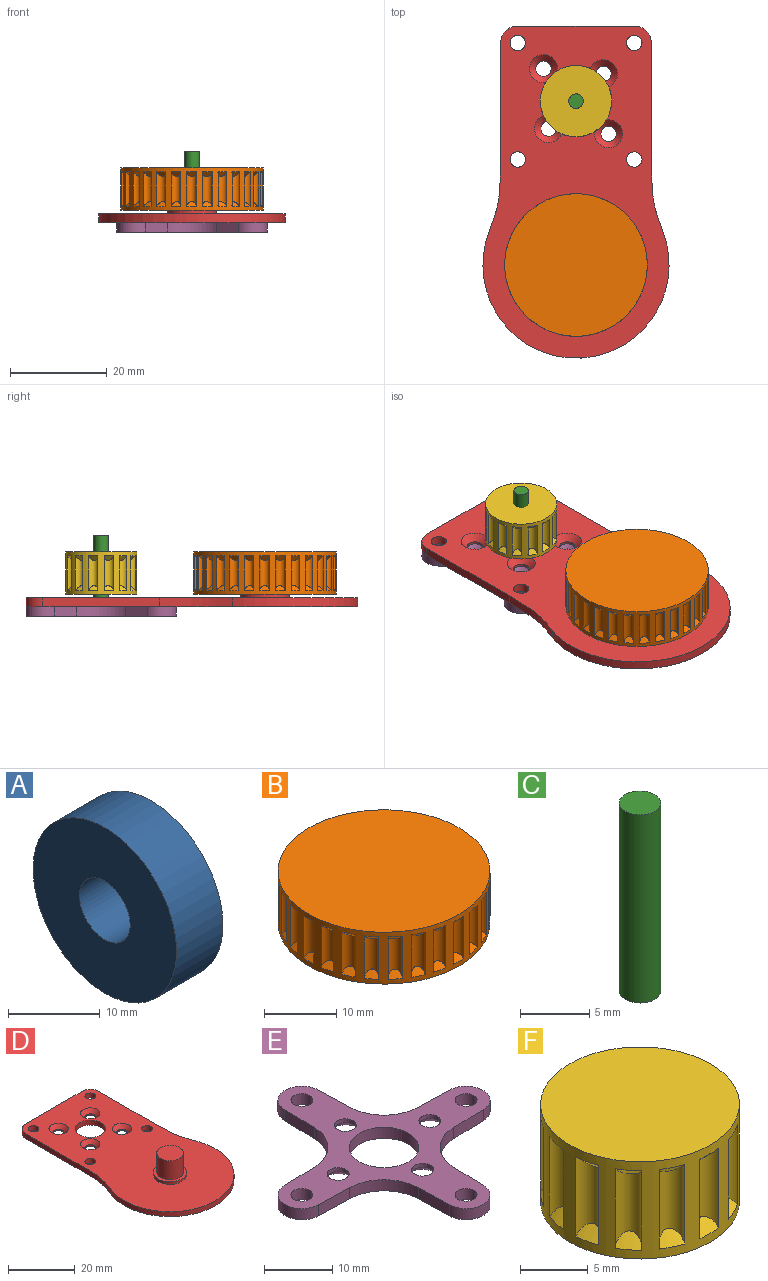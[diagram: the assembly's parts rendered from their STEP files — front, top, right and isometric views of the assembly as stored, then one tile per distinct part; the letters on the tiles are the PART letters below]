
ASSEMBLY  parts=6 mates=5
PART A: 4 faces, bbox 7.2x22.1x22.1 mm
  f0: cylinder r=3.91mm len=7.81mm, axis (-1,0,0), area 175.4mm2, adj f2,f3
  f1: cylinder r=11.05mm len=22.1mm, axis (-1,0,0), area 496.4mm2, adj f2,f3
  f2: plane 22.1x22.1mm, normal (1,0,0), area 335.7mm2, adj f0,f1
  f3: plane 22.1x22.1mm, normal (-1,0,0), area 335.7mm2, adj f0,f1
PART B: 87 faces, bbox 29.4x29.4x8.8 mm
  f0: cylinder r=1mm len=7.2mm, axis (0,0,-1), area 18.2mm2, adj f28,f29,f58
  f1: cylinder r=1mm len=7.2mm, axis (0,0,-1), area 18.2mm2, adj f28,f30,f59
  f2: cylinder r=1mm len=7.2mm, axis (0,0,-1), area 18.2mm2, adj f28,f31,f60
  f3: cylinder r=1mm len=7.2mm, axis (0,0,-1), area 18.2mm2, adj f28,f32,f61
  f4: cylinder r=1mm len=7.2mm, axis (0,0,-1), area 18.2mm2, adj f28,f33,f62
  f5: cylinder r=1mm len=7.2mm, axis (0,0,-1), area 18.2mm2, adj f28,f34,f63
  f6: cylinder r=1mm len=7.2mm, axis (0,0,-1), area 18.2mm2, adj f28,f35,f64
  f7: cylinder r=1mm len=7.2mm, axis (0,0,-1), area 18.2mm2, adj f28,f36,f65
  f8: cylinder r=1mm len=7.2mm, axis (0,0,-1), area 18.2mm2, adj f28,f37,f66
  f9: cylinder r=1mm len=7.2mm, axis (0,0,-1), area 18.2mm2, adj f28,f38,f67
  f10: cylinder r=1mm len=7.2mm, axis (0,0,-1), area 18.2mm2, adj f28,f39,f68
  f11: cylinder r=1mm len=7.2mm, axis (0,0,-1), area 18.2mm2, adj f28,f40,f69
  f12: cylinder r=1mm len=7.2mm, axis (0,0,-1), area 18.2mm2, adj f28,f41,f70
  f13: cylinder r=1mm len=7.2mm, axis (0,0,-1), area 18.2mm2, adj f28,f42,f71
  f14: cylinder r=1mm len=7.2mm, axis (0,0,-1), area 18.2mm2, adj f28,f43,f72
  f15: cylinder r=1mm len=7.2mm, axis (0,0,-1), area 18.2mm2, adj f28,f44,f73
  f16: cylinder r=1mm len=7.2mm, axis (0,0,-1), area 18.2mm2, adj f28,f45,f74
  f17: cylinder r=1mm len=7.2mm, axis (0,0,-1), area 18.2mm2, adj f28,f46,f75
  f18: cylinder r=1mm len=7.2mm, axis (0,0,-1), area 18.2mm2, adj f28,f47,f76
  f19: cylinder r=1mm len=7.2mm, axis (0,0,-1), area 18.2mm2, adj f28,f48,f77
  f20: cylinder r=1mm len=7.2mm, axis (0,0,-1), area 18.2mm2, adj f28,f49,f78
  f21: cylinder r=1mm len=7.2mm, axis (0,0,-1), area 18.2mm2, adj f28,f50,f79
  f22: cylinder r=1mm len=7.2mm, axis (0,0,-1), area 18.2mm2, adj f28,f51,f80
  f23: cylinder r=1mm len=7.2mm, axis (0,0,-1), area 18.2mm2, adj f28,f52,f81
  f24: cylinder r=1mm len=7.2mm, axis (0,0,-1), area 18.2mm2, adj f28,f53,f82
  f25: cylinder r=1mm len=7.2mm, axis (0,0,-1), area 18.2mm2, adj f28,f54,f83
  f26: cylinder r=1mm len=7.2mm, axis (0,0,-1), area 18.2mm2, adj f28,f55,f84
  f27: cylinder r=1mm len=7.2mm, axis (0,0,-1), area 18.2mm2, adj f28,f56,f85
  f28: cylinder r=14.71mm len=29.41mm, axis (0,0,-1), area 409.8mm2, adj f0,f1,f2,f3,f4,f5,f6,f7
  f29: cone r=14.71mm half-angle=45deg, axis (0,0,-1), area 2.2mm2, adj f0,f28
  f30: cone r=14.71mm half-angle=45deg, axis (0,0,-1), area 2.2mm2, adj f1,f28
  f31: cone r=14.71mm half-angle=45deg, axis (0,0,-1), area 2.2mm2, adj f2,f28
  f32: cone r=14.71mm half-angle=45deg, axis (0,0,-1), area 2.2mm2, adj f3,f28
  f33: cone r=14.71mm half-angle=45deg, axis (0,0,-1), area 2.2mm2, adj f4,f28
  f34: cone r=14.71mm half-angle=45deg, axis (0,0,-1), area 2.2mm2, adj f5,f28
  f35: cone r=14.71mm half-angle=45deg, axis (0,0,-1), area 2.2mm2, adj f6,f28
  f36: cone r=14.71mm half-angle=45deg, axis (0,0,-1), area 2.2mm2, adj f7,f28
  f37: cone r=14.71mm half-angle=45deg, axis (0,0,-1), area 2.2mm2, adj f8,f28
  f38: cone r=14.71mm half-angle=45deg, axis (0,0,-1), area 2.2mm2, adj f9,f28
  f39: cone r=14.71mm half-angle=45deg, axis (0,0,-1), area 2.2mm2, adj f10,f28
  f40: cone r=14.71mm half-angle=45deg, axis (0,0,-1), area 2.2mm2, adj f11,f28
  f41: cone r=14.71mm half-angle=45deg, axis (0,0,-1), area 2.2mm2, adj f12,f28
  f42: cone r=14.71mm half-angle=45deg, axis (0,0,-1), area 2.2mm2, adj f13,f28
  f43: cone r=14.71mm half-angle=45deg, axis (0,0,-1), area 2.2mm2, adj f14,f28
  f44: cone r=14.71mm half-angle=45deg, axis (0,0,-1), area 2.2mm2, adj f15,f28
  f45: cone r=14.71mm half-angle=45deg, axis (0,0,-1), area 2.2mm2, adj f16,f28
  f46: cone r=14.71mm half-angle=45deg, axis (0,0,-1), area 2.2mm2, adj f17,f28
  f47: cone r=14.71mm half-angle=45deg, axis (0,0,-1), area 2.2mm2, adj f18,f28
  f48: cone r=14.71mm half-angle=45deg, axis (0,0,-1), area 2.2mm2, adj f19,f28
  f49: cone r=14.71mm half-angle=45deg, axis (0,0,-1), area 2.2mm2, adj f20,f28
  f50: cone r=14.71mm half-angle=45deg, axis (0,0,-1), area 2.2mm2, adj f21,f28
  f51: cone r=14.71mm half-angle=45deg, axis (0,0,-1), area 2.2mm2, adj f22,f28
  f52: cone r=14.71mm half-angle=45deg, axis (0,0,-1), area 2.2mm2, adj f23,f28
  f53: cone r=14.71mm half-angle=45deg, axis (0,0,-1), area 2.2mm2, adj f24,f28
  f54: cone r=14.71mm half-angle=45deg, axis (0,0,-1), area 2.2mm2, adj f25,f28
  f55: cone r=14.71mm half-angle=45deg, axis (0,0,-1), area 2.2mm2, adj f26,f28
  f56: cone r=14.71mm half-angle=45deg, axis (0,0,-1), area 2.2mm2, adj f27,f28
  f57: plane 29.41x29.41mm, normal (0,0,-1), area 679.4mm2, adj f28
  f58: cone r=14.71mm half-angle=45deg, axis (0,0,1), area 2.2mm2, adj f0,f28
  f59: cone r=14.71mm half-angle=45deg, axis (0,0,1), area 2.2mm2, adj f1,f28
  f60: cone r=14.71mm half-angle=45deg, axis (0,0,1), area 2.2mm2, adj f2,f28
  f61: cone r=14.71mm half-angle=45deg, axis (0,0,1), area 2.2mm2, adj f3,f28
  f62: cone r=14.71mm half-angle=45deg, axis (0,0,1), area 2.2mm2, adj f4,f28
  f63: cone r=14.71mm half-angle=45deg, axis (0,0,1), area 2.2mm2, adj f5,f28
  f64: cone r=14.71mm half-angle=45deg, axis (0,0,1), area 2.2mm2, adj f6,f28
  f65: cone r=14.71mm half-angle=45deg, axis (0,0,1), area 2.2mm2, adj f7,f28
  f66: cone r=14.71mm half-angle=45deg, axis (0,0,1), area 2.2mm2, adj f8,f28
  f67: cone r=14.71mm half-angle=45deg, axis (0,0,1), area 2.2mm2, adj f9,f28
  f68: cone r=14.71mm half-angle=45deg, axis (0,0,1), area 2.2mm2, adj f10,f28
  f69: cone r=14.71mm half-angle=45deg, axis (0,0,1), area 2.2mm2, adj f11,f28
  f70: cone r=14.71mm half-angle=45deg, axis (0,0,1), area 2.2mm2, adj f12,f28
  f71: cone r=14.71mm half-angle=45deg, axis (0,0,1), area 2.2mm2, adj f13,f28
  f72: cone r=14.71mm half-angle=45deg, axis (0,0,1), area 2.2mm2, adj f14,f28
  f73: cone r=14.71mm half-angle=45deg, axis (0,0,1), area 2.2mm2, adj f15,f28
  f74: cone r=14.71mm half-angle=45deg, axis (0,0,1), area 2.2mm2, adj f16,f28
  f75: cone r=14.71mm half-angle=45deg, axis (0,0,1), area 2.2mm2, adj f17,f28
  f76: cone r=14.71mm half-angle=45deg, axis (0,0,1), area 2.2mm2, adj f18,f28
  f77: cone r=14.71mm half-angle=45deg, axis (0,0,1), area 2.2mm2, adj f19,f28
  f78: cone r=14.71mm half-angle=45deg, axis (0,0,1), area 2.2mm2, adj f20,f28
  f79: cone r=14.71mm half-angle=45deg, axis (0,0,1), area 2.2mm2, adj f21,f28
  f80: cone r=14.71mm half-angle=45deg, axis (0,0,1), area 2.2mm2, adj f22,f28
  f81: cone r=14.71mm half-angle=45deg, axis (0,0,1), area 2.2mm2, adj f23,f28
  f82: cone r=14.71mm half-angle=45deg, axis (0,0,1), area 2.2mm2, adj f24,f28
  f83: cone r=14.71mm half-angle=45deg, axis (0,0,1), area 2.2mm2, adj f25,f28
  f84: cone r=14.71mm half-angle=45deg, axis (0,0,1), area 2.2mm2, adj f26,f28
  f85: cone r=14.71mm half-angle=45deg, axis (0,0,1), area 2.2mm2, adj f27,f28
  f86: plane 29.41x29.41mm, normal (0,0,1), area 679.4mm2, adj f28
PART C: 3 faces, bbox 3x3x16.6 mm
  f0: cylinder r=1.5mm len=16.6mm, axis (0,0,1), area 156.5mm2, adj f1,f2
  f1: plane 3x3mm, normal (0,0,-1), area 7.1mm2, adj f0
  f2: plane 3x3mm, normal (0,0,1), area 7.1mm2, adj f0
PART D: 27 faces, bbox 38.4x68.5x9.8 mm
  f0: plane 24.04x1.8mm, normal (-1,0,0), area 43.3mm2, adj f1,f14,f17,f18
  f1: extruded ~15.15x2.5mm, area 27.9mm2, adj f0,f2,f17,f18
  f2: cylinder r=19.21mm len=38.41mm, axis (0,0,-1), area 133mm2, adj f1,f3,f17,f18
  f3: extruded ~15.15x2.5mm, area 27.9mm2, adj f2,f4,f17,f18
  f4: plane 24.04x1.8mm, normal (1,0,0), area 43.3mm2, adj f3,f5,f17,f18
  f5: cylinder r=3.5mm len=3.5mm, axis (0,0,-1), area 9.9mm2, adj f4,f6,f17,f18
  f6: plane 24.04x1.8mm, normal (0,1,0), area 43.3mm2, adj f5,f14,f17,f18
  f7: cylinder r=1.6mm len=3.2mm, axis (0,0,-1), area 5mm2, adj f18,f25
  f8: cylinder r=1.6mm len=3.2mm, axis (0,0,-1), area 5mm2, adj f18,f23
  f9: cylinder r=1.6mm len=3.2mm, axis (0,0,-1), area 5mm2, adj f18,f24
  f10: cylinder r=1.6mm len=3.2mm, axis (0,0,-1), area 5mm2, adj f18,f26
  f11: cylinder r=1.6mm len=3.2mm, axis (0,0,-1), area 18.1mm2, adj f17,f18
  f12: cylinder r=1.6mm len=3.2mm, axis (0,0,-1), area 18.1mm2, adj f17,f18
  f13: cylinder r=1.6mm len=3.2mm, axis (0,0,-1), area 18.1mm2, adj f17,f18
  f14: cylinder r=3.5mm len=3.5mm, axis (0,0,-1), area 9.9mm2, adj f0,f6,f17,f18
  f15: cylinder r=1.6mm len=3.2mm, axis (0,0,-1), area 18.1mm2, adj f17,f18
  f16: cylinder r=4.5mm len=9mm, axis (0,0,-1), area 50.9mm2, adj f17,f18
  f17: plane 68.54x38.41mm, normal (0,0,1), area 1889.5mm2, adj f0,f1,f2,f3,f4,f5,f6,f11
  f18: plane 68.54x38.41mm, normal (0,0,-1), area 2041.6mm2, adj f0,f1,f2,f3,f4,f5,f6,f7
  f19: cylinder r=5mm len=10mm, axis (0,0,-1), area 31.4mm2, adj f17,f20
  f20: plane 10x10mm, normal (0,0,1), area 28.3mm2, adj f19,f22
  f21: plane 8x8mm, normal (0,0,1), area 50.3mm2, adj f22
  f22: cylinder r=4mm len=8mm, axis (0,0,-1), area 175.9mm2, adj f20,f21
  f23: cone r=1.6mm half-angle=45deg, axis (0,0,1), area 26mm2, adj f8,f17
  f24: cone r=1.6mm half-angle=45deg, axis (0,0,1), area 26mm2, adj f9,f17
  f25: cone r=1.6mm half-angle=45deg, axis (0,0,1), area 26mm2, adj f7,f17
  f26: cone r=1.6mm half-angle=45deg, axis (0,0,1), area 26mm2, adj f10,f17
PART E: 31 faces, bbox 41x41x2 mm
  f0: cylinder r=3.5mm len=7mm, axis (0,0,-1), area 21.7mm2, adj f1,f24,f25,f26
  f1: plane 6.3x2mm, normal (-1,0.02,0), area 12.6mm2, adj f0,f2,f25,f26
  f2: cylinder r=7.31mm len=7.13mm, axis (0,0,-1), area 22.3mm2, adj f1,f3,f25,f26
  f3: plane 6.3x2mm, normal (-0.02,1,0), area 12.6mm2, adj f2,f4,f25,f26
  f4: cylinder r=3.5mm len=7mm, axis (0,0,-1), area 21.7mm2, adj f3,f5,f25,f26
  f5: plane 6.3x2mm, normal (-0.02,-1,0), area 12.6mm2, adj f4,f6,f25,f26
  f6: cylinder r=7.31mm len=7.13mm, axis (0,0,-1), area 22.3mm2, adj f5,f7,f25,f26
  f7: plane 6.3x2mm, normal (-1,-0.02,0), area 12.6mm2, adj f6,f8,f25,f26
  f8: cylinder r=3.5mm len=7mm, axis (0,0,-1), area 21.7mm2, adj f7,f9,f25,f26
  f9: plane 6.3x2mm, normal (1,-0.02,0), area 12.6mm2, adj f8,f10,f25,f26
  f10: cylinder r=7.31mm len=7.13mm, axis (0,0,-1), area 22.3mm2, adj f9,f11,f25,f26
  f11: plane 6.3x2mm, normal (0.02,-1,0), area 12.6mm2, adj f10,f12,f25,f26
  f12: cylinder r=3.5mm len=7mm, axis (0,0,-1), area 21.7mm2, adj f11,f13,f25,f26
  f13: plane 6.3x2mm, normal (0.02,1,0), area 12.6mm2, adj f12,f14,f25,f26
  f14: cylinder r=7.31mm len=7.13mm, axis (0,0,-1), area 22.3mm2, adj f13,f24,f25,f26
  f15: cylinder r=1.6mm len=3.2mm, axis (0,0,-1), area 7mm2, adj f25,f30
  f16: cylinder r=1.6mm len=3.2mm, axis (0,0,-1), area 7mm2, adj f25,f29
  f17: cylinder r=1.6mm len=3.2mm, axis (0,0,-1), area 20.1mm2, adj f25,f26
  f18: cylinder r=1.6mm len=3.2mm, axis (0,0,-1), area 20.1mm2, adj f25,f26
  f19: cylinder r=5.1mm len=10.2mm, axis (0,0,-1), area 64.1mm2, adj f25,f26
  f20: cylinder r=1.6mm len=3.2mm, axis (0,0,-1), area 20.1mm2, adj f25,f26
  f21: cylinder r=1.6mm len=3.2mm, axis (0,0,-1), area 20.1mm2, adj f25,f26
  f22: cylinder r=1.6mm len=3.2mm, axis (0,0,-1), area 7mm2, adj f25,f27
  f23: cylinder r=1.6mm len=3.2mm, axis (0,0,-1), area 7mm2, adj f25,f28
  f24: plane 6.3x2mm, normal (1,0.02,0), area 12.6mm2, adj f0,f14,f25,f26
  f25: plane 41x41mm, normal (0,0,1), area 416.3mm2, adj f0,f1,f2,f3,f4,f5,f6,f7
  f26: plane 41x41mm, normal (0,0,-1), area 342.7mm2, adj f0,f1,f2,f3,f4,f5,f6,f7
  f27: cone r=2.9mm half-angle=45deg, axis (0,0,-1), area 26mm2, adj f22,f26
  f28: cone r=1.6mm half-angle=45deg, axis (0,0,-1), area 26mm2, adj f23,f26
  f29: cone r=1.6mm half-angle=45deg, axis (0,0,-1), area 26mm2, adj f16,f26
  f30: cone r=2.9mm half-angle=45deg, axis (0,0,-1), area 26mm2, adj f15,f26
PART F: 45 faces, bbox 14.7x14.7x8.8 mm
  f0: cylinder r=1mm len=7.2mm, axis (0,0,-1), area 17.9mm2, adj f14,f15,f30
  f1: cylinder r=1mm len=7.2mm, axis (0,0,-1), area 17.9mm2, adj f14,f16,f31
  f2: cylinder r=1mm len=7.2mm, axis (0,0,-1), area 17.9mm2, adj f14,f17,f32
  f3: cylinder r=1mm len=7.2mm, axis (0,0,-1), area 17.9mm2, adj f14,f18,f33
  f4: cylinder r=1mm len=7.2mm, axis (0,0,-1), area 17.9mm2, adj f14,f19,f34
  f5: cylinder r=1mm len=7.2mm, axis (0,0,-1), area 17.9mm2, adj f14,f20,f35
  f6: cylinder r=1mm len=7.2mm, axis (0,0,-1), area 17.9mm2, adj f14,f21,f36
  f7: cylinder r=1mm len=7.2mm, axis (0,0,-1), area 17.9mm2, adj f14,f22,f37
  f8: cylinder r=1mm len=7.2mm, axis (0,0,-1), area 17.9mm2, adj f14,f23,f38
  f9: cylinder r=1mm len=7.2mm, axis (0,0,-1), area 17.9mm2, adj f14,f24,f39
  f10: cylinder r=1mm len=7.2mm, axis (0,0,-1), area 17.9mm2, adj f14,f25,f40
  f11: cylinder r=1mm len=7.2mm, axis (0,0,-1), area 17.9mm2, adj f14,f26,f41
  f12: cylinder r=1mm len=7.2mm, axis (0,0,-1), area 17.9mm2, adj f14,f27,f42
  f13: cylinder r=1mm len=7.2mm, axis (0,0,-1), area 17.9mm2, adj f14,f28,f43
  f14: cylinder r=7.35mm len=14.71mm, axis (0,0,-1), area 204.8mm2, adj f0,f1,f2,f3,f4,f5,f6,f7
  f15: cone r=7.35mm half-angle=45deg, axis (0,0,-1), area 2.2mm2, adj f0,f14
  f16: cone r=7.35mm half-angle=45deg, axis (0,0,-1), area 2.2mm2, adj f1,f14
  f17: cone r=7.35mm half-angle=45deg, axis (0,0,-1), area 2.2mm2, adj f2,f14
  f18: cone r=7.35mm half-angle=45deg, axis (0,0,-1), area 2.2mm2, adj f3,f14
  f19: cone r=7.35mm half-angle=45deg, axis (0,0,-1), area 2.2mm2, adj f4,f14
  f20: cone r=7.35mm half-angle=45deg, axis (0,0,-1), area 2.2mm2, adj f5,f14
  f21: cone r=7.35mm half-angle=45deg, axis (0,0,-1), area 2.2mm2, adj f6,f14
  f22: cone r=7.35mm half-angle=45deg, axis (0,0,-1), area 2.2mm2, adj f7,f14
  f23: cone r=7.35mm half-angle=45deg, axis (0,0,-1), area 2.2mm2, adj f8,f14
  f24: cone r=7.35mm half-angle=45deg, axis (0,0,-1), area 2.2mm2, adj f9,f14
  f25: cone r=7.35mm half-angle=45deg, axis (0,0,-1), area 2.2mm2, adj f10,f14
  f26: cone r=7.35mm half-angle=45deg, axis (0,0,-1), area 2.2mm2, adj f11,f14
  f27: cone r=7.35mm half-angle=45deg, axis (0,0,-1), area 2.2mm2, adj f12,f14
  f28: cone r=7.35mm half-angle=45deg, axis (0,0,-1), area 2.2mm2, adj f13,f14
  f29: plane 14.71x14.71mm, normal (0,0,-1), area 169.9mm2, adj f14
  f30: cone r=7.35mm half-angle=45deg, axis (0,0,1), area 2.2mm2, adj f0,f14
  f31: cone r=7.35mm half-angle=45deg, axis (0,0,1), area 2.2mm2, adj f1,f14
  f32: cone r=7.35mm half-angle=45deg, axis (0,0,1), area 2.2mm2, adj f2,f14
  f33: cone r=7.35mm half-angle=45deg, axis (0,0,1), area 2.2mm2, adj f3,f14
  f34: cone r=7.35mm half-angle=45deg, axis (0,0,1), area 2.2mm2, adj f4,f14
  f35: cone r=7.35mm half-angle=45deg, axis (0,0,1), area 2.2mm2, adj f5,f14
  f36: cone r=7.35mm half-angle=45deg, axis (0,0,1), area 2.2mm2, adj f6,f14
  f37: cone r=7.35mm half-angle=45deg, axis (0,0,1), area 2.2mm2, adj f7,f14
  f38: cone r=7.35mm half-angle=45deg, axis (0,0,1), area 2.2mm2, adj f8,f14
  f39: cone r=7.35mm half-angle=45deg, axis (0,0,1), area 2.2mm2, adj f9,f14
  f40: cone r=7.35mm half-angle=45deg, axis (0,0,1), area 2.2mm2, adj f10,f14
  f41: cone r=7.35mm half-angle=45deg, axis (0,0,1), area 2.2mm2, adj f11,f14
  f42: cone r=7.35mm half-angle=45deg, axis (0,0,1), area 2.2mm2, adj f12,f14
  f43: cone r=7.35mm half-angle=45deg, axis (0,0,1), area 2.2mm2, adj f13,f14
  f44: plane 14.71x14.71mm, normal (0,0,1), area 169.9mm2, adj f14
PLACE A rot(axis=(0,-1,0),90deg) t=(24.65,0,0.02)mm
PLACE B at identity
PLACE C rot(axis=(0,0,-1),45deg) t=(0,33.81,9.3)mm
PLACE D t=(0,33.81,-3.3)mm
PLACE E rot(axis=(-0.92,0.38,0),180deg) t=(0,33.81,-3.3)mm
PLACE F at identity
MATE revolute D.f5 <-> E.f21  axis (0,0,-1) through (12.02,45.83,-3.3)mm
MATE revolute D.f11 <-> E.f4  axis (0,0,-1) through (-12.02,45.83,-3.3)mm
MATE revolute E.f19 <-> F.f14  axis (0,0,1) through (0,33.81,-3.3)mm
MATE revolute A.f0 <-> B.f28  axis (0,0,-1) through (0,0,3.6)mm
MATE fastened C.f0 <-> E.f19  axis (0,0,-1) through (0,33.81,-5.3)mm
